FCSTD DOCUMENT  (FreeCAD 0.14R3703 (Git))
Label: 5x3 shredder
License: CC-BY 3.0
LicenseURL: http://creativecommons.org/licenses/by/3.0/
objects: Sketcher::SketchObject×7
note: 7 computed .brp shape members not serialized (recipe doc carries the construction recipe); baked Part::Feature solids carry a one-line shape summary decoded from their .brp

FEATURE [Sketcher::SketchObject] Sketch003  label="stemline quad I"
  Placement = pos=(0,0,0) rot=(0.57735,0.57735,0.57735;2.0944rad)
  sketch-geometry (3):
    g0: LineSegment StartX=40 StartY=60 StartZ=0 EndX=30 EndY=33.4055 EndZ=0
    g1: LineSegment StartX=30 StartY=33.4055 StartZ=0 EndX=20 EndY=20 EndZ=0
    g2: LineSegment StartX=20 StartY=20 StartZ=0 EndX=0 EndY=0 EndZ=0
  constraints (2):
    c: Coincident(g0,g1)
    c: Coincident(g1,g2)
FEATURE [Sketcher::SketchObject] Sketch004  label="crossSection1 quad I"
  Placement = pos=(0,0,0) rot=(1,0,0;1.5708rad)
  sketch-geometry (3):
    g0: LineSegment StartX=30 StartY=60 StartZ=0 EndX=26.3533 EndY=32.1683 EndZ=0
    g1: LineSegment StartX=26.3533 StartY=32.1683 StartZ=0 EndX=16.7028 EndY=14.8469 EndZ=0
    g2: LineSegment StartX=16.7028 StartY=14.8469 StartZ=0 EndX=0 EndY=0 EndZ=0
  constraints (2):
    c: Coincident(g0,g1)
    c: Coincident(g1,g2)
FEATURE [Sketcher::SketchObject] Sketch005  label="crossSection2 quad I"
  Placement = pos=(0,-35,0) rot=(1,0,0;1.5708rad)
  sketch-geometry (3):
    g0: LineSegment StartX=30 StartY=60 StartZ=0 EndX=26.3533 EndY=32.1683 EndZ=0
    g1: LineSegment StartX=26.3533 StartY=32.1683 StartZ=0 EndX=16.7028 EndY=14.8469 EndZ=0
    g2: LineSegment StartX=16.7028 StartY=14.8469 StartZ=0 EndX=0 EndY=0 EndZ=0
  constraints (2):
    c: Coincident(g0,g1)
    c: Coincident(g1,g2)
FEATURE [Sketcher::SketchObject] Sketch006  label="transom quad IV"
  Placement = pos=(0,-105,0) rot=(0,0,1;0rad)
  sketch-geometry (3):
    g0: LineSegment StartX=30 StartY=-35.1377 StartZ=0 EndX=25.3635 EndY=-46.7677 EndZ=0
    g1: LineSegment StartX=25.3635 StartY=-46.7677 StartZ=0 EndX=12.2487 EndY=-52.7065 EndZ=0
    g2: LineSegment StartX=12.2487 StartY=-52.7065 StartZ=0 EndX=0 EndY=-54.4386 EndZ=0
  constraints (2):
    c: Coincident(g0,g1)
    c: Coincident(g1,g2)
FEATURE [Sketcher::SketchObject] Sketch007  label="crossSection4 quad I"
  Placement = pos=(0,-105,0) rot=(1,0,0;1.5708rad)
  sketch-geometry (3):
    g0: LineSegment StartX=30 StartY=60 StartZ=0 EndX=26.3533 EndY=32.1683 EndZ=0
    g1: LineSegment StartX=26.3533 StartY=32.1683 StartZ=0 EndX=16.7028 EndY=14.8469 EndZ=0
    g2: LineSegment StartX=16.7028 StartY=14.8469 StartZ=0 EndX=0 EndY=0 EndZ=0
  constraints (2):
    c: Coincident(g0,g1)
    c: Coincident(g1,g2)
FEATURE [Sketcher::SketchObject] Sketch008  label="crossSection5 quad I"
  Placement = pos=(0,-140,0) rot=(1,0,0;1.5708rad)
  sketch-geometry (3):
    g0: LineSegment StartX=30 StartY=60 StartZ=0 EndX=26.3533 EndY=32.1683 EndZ=0
    g1: LineSegment StartX=26.3533 StartY=32.1683 StartZ=0 EndX=16.7028 EndY=14.8469 EndZ=0
    g2: LineSegment StartX=16.7028 StartY=14.8469 StartZ=0 EndX=0 EndY=0 EndZ=0
  constraints (2):
    c: Coincident(g0,g1)
    c: Coincident(g1,g2)
FEATURE [Sketcher::SketchObject] Sketch009  label="crossSection3 quad I"
  Placement = pos=(0,-75,0) rot=(1,0,0;1.5708rad)
  sketch-geometry (3):
    g0: LineSegment StartX=0.249166 StartY=0.249166 StartZ=0 EndX=18.1187 EndY=13.9139 EndZ=0
    g1: LineSegment StartX=18.1187 StartY=13.9139 StartZ=0 EndX=28.2956 EndY=31.8056 EndZ=0
    g2: LineSegment StartX=28.2956 StartY=31.8056 StartZ=0 EndX=31.5785 EndY=59.7101 EndZ=0
  constraints (2):
    c: Coincident(g0,g1)
    c: Coincident(g1,g2)
